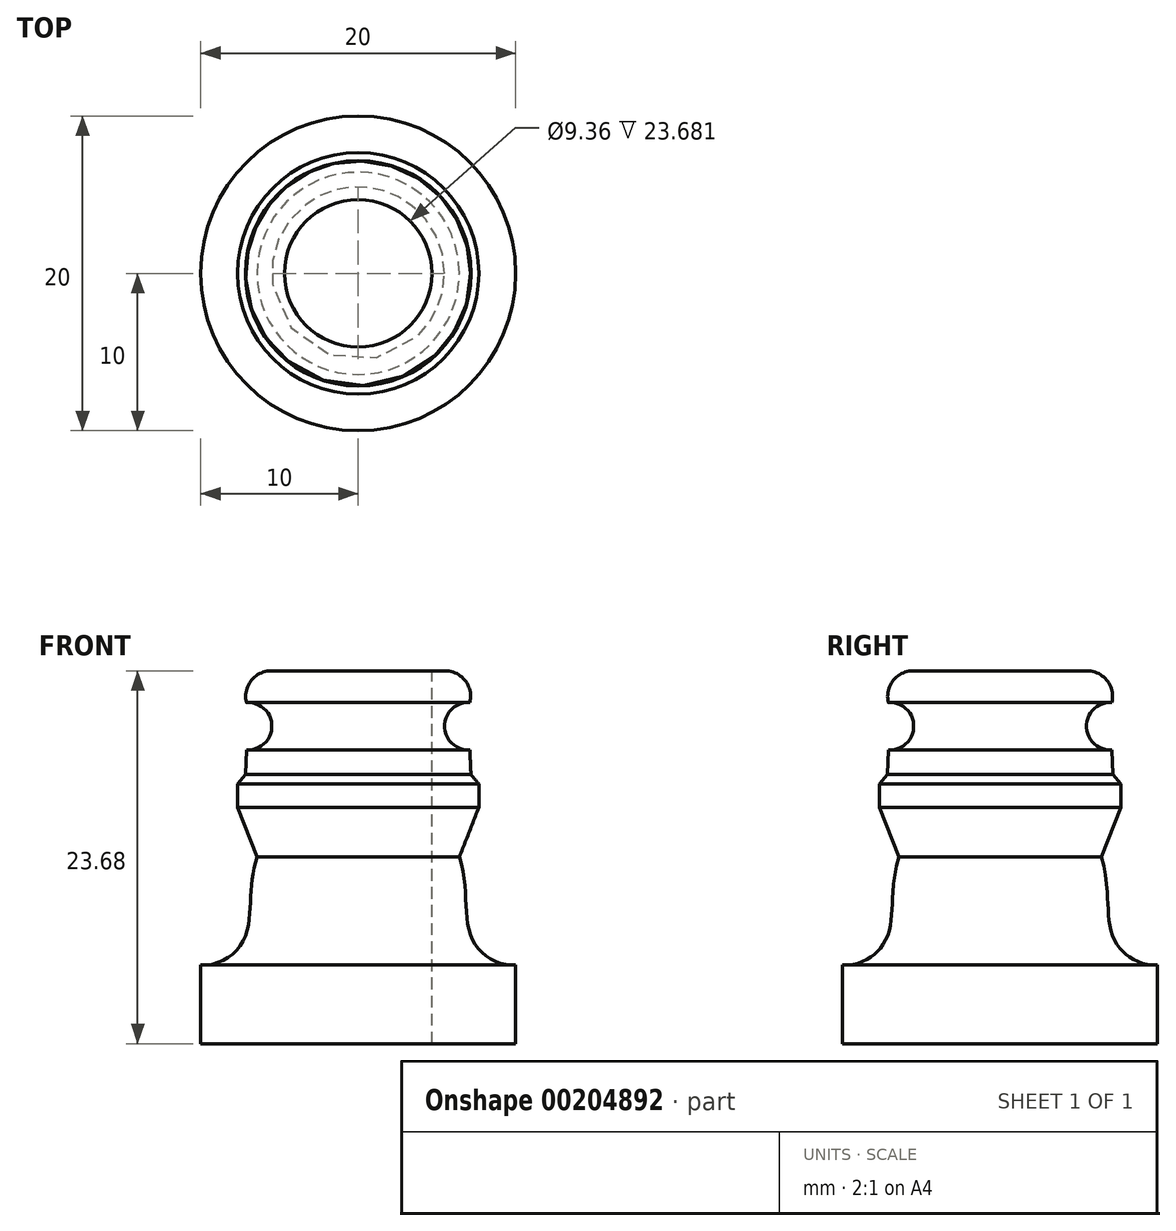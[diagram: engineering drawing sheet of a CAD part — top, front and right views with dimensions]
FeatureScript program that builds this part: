
annotation { "Feature Type Name" : "Feature", "Feature Type Description" : "" }
export const myFeature = defineFeature(function(context is Context, id is Id, definition is map)
    precondition{}
    {
        {
            var Q0;
            Q0=qCreatedBy(makeId("Front.planeOp"),FACE);
            var sketch = newSketch(context, id + "F0", { "sketchPlane" : qUnion([Q0])});
            skLineSegment(sketch, "E0", {"start": v(4.68, 11.83) * mm, "end": v(5.53, 11.83) * mm});
            skPoint(sketch, "E1", {"position": v(7.1, 9.82) * mm});
            skPoint(sketch, "E2.orphan", {"position": v(5.53, 7.97) * mm});
            skArc(sketch, "E3", {"start": v(7.1, 9.82) * mm, "mid": v(5.49, 8.32) * mm, "end": v(7.1, 6.82) * mm});
            skLineSegment(sketch, "E4", {"start": v(7.16, 5.24) * mm, "end": v(7.66, 4.65) * mm});
            skLineSegment(sketch, "E5", {"start": v(7.66, 4.65) * mm, "end": v(7.66, 3.15) * mm});
            skLineSegment(sketch, "E6", {"start": v(7.66, 3.15) * mm, "end": v(6.42, 0) * mm});
            skFitSpline(sketch, "E7", {"points": [v(6.42, 0) * mm, v(7.25, -5.24) * mm, v(10, -6.85) * mm], "startDerivative": vector(3.45, -10.54) * mm, "endDerivative": vector(7.47, 0.57) * mm});
            skLineSegment(sketch, "E8", {"start": v(10, -6.85) * mm, "end": v(10, -11.85) * mm});
            skLineSegment(sketch, "E9", {"start": v(10, -11.85) * mm, "end": v(4.68, -11.85) * mm});
            skLineSegment(sketch, "E10", {"start": v(4.68, -11.85) * mm, "end": v(4.68, 11.83) * mm});
            skPoint(sketch, "E11.end.orphan", {"position": v(0, 11.83) * mm});
            skLineSegment(sketch, "E12", {"start": v(0, 11.83) * mm, "end": v(0, -10.27) * mm});
            skLineSegment(sketch, "E13", {"start": v(7.1, 6.82) * mm, "end": v(7.16, 5.24) * mm});
            skArc(sketch, "E14", {"start": v(5.53, 11.83) * mm, "mid": v(6.8, 11.2) * mm, "end": v(7.1, 9.82) * mm});
            skSolve(sketch);
        }
        {
            var Q0;
            Q0=makeQuery(id+"F0.imprint","IMPRINT",FACE,{"disambiguationData":[TD([[makeQuery(id+"F0.imprint","IMPRINT",EDGE,{"derivedFrom":sQuery(id+"F0.wireOp",EDGE,"E0")}),-1.0]])]});
            var Q1;
            Q1=sQuery(id+"F0.wireOp",EDGE,"E12");
            revolve(context, id + "F1", {"entities" : qUnion([Q0]), "axis" : qUnion([Q1]), "revolveType" : RevolveType.FULL});
        }
    });
